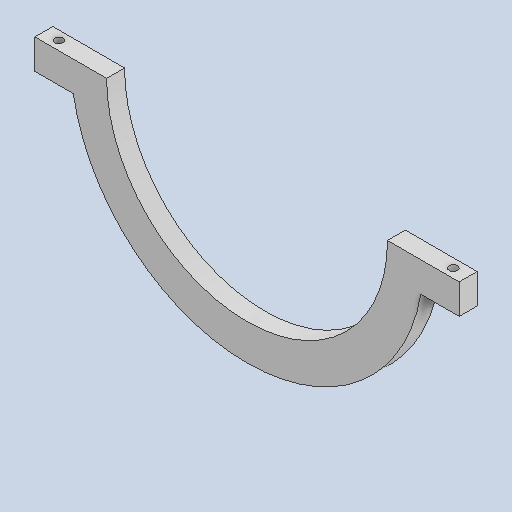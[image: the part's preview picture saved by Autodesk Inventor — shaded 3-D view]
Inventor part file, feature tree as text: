
AUTODESK INVENTOR PART (.ipt)
format: ipt  version: 2025 (Build 290162010, 162A)  size: 178,688 bytes
history: native  units: mm
features: sketch x4, hole x3, extrude x1, fillet x1, pattern_circular x1, mirror x1, other x1
ambient origin geometry x8: Origin, YZ Plane, XZ Plane, XY Plane, X Axis, Y Axis, Z Axis, Center Point
bodies: Solid1 (feature_tree)
feature tree (12):
  extrude  "Extrusion1"  Depth=30.0mm
  sketch  "Sketch4"  dims[d27=265.0mm d35=1.963495mm]
  sketch  "Sketch7"  dims[d36=60.0mm d40=60.0mm d41=50.0mm]
  fillet  "Fillet2"  Radius=80.0mm
  hole  "Hole1"  [1 undecoded]
  hole  "Hole2"  [1 undecoded]
  pattern_circular  "Circular Pattern4"  Count=5  [1 undecoded]
  hole  "Hole3"  [1 undecoded]
  mirror  "Mirror1"
  sketch  "Sketch1"  dims[d2=30.0mm d3=0.0mm d13=530.0mm d26=80.0mm]
  sketch  "Sketch8"  dims[d42=25.0mm d46=14.0mm d47=32.0mm d48=24.0mm d49=15.0mm d50=90.0deg d51=8.0mm d52=20.594885mm d53=14.0mm d54=6.0mm d55=24.0mm d56=15.0mm d57=90.0deg d58=8.0mm d59=20.594885mm d60=90.0mm d61=180.0deg d63=25.0mm d64=14.0mm d65=6.0mm d66=4.0mm d67=2.0mm d68=90.0deg d69=8.0mm d70=20.594885mm d71=10.0mm]
  other  "Definition1"
note: 4 required parameter values undecoded (feature->parameter linkage not recoverable at this tier; creation-order binding heuristic only, values carry confidence <= 0.55)
